# Revit family: HL_Dachablauf_HL64.1F-B-221103
name_source: partatom
category: Instalační zařizovací předměty
units: mm (PartAtom-declared; Revit-internal decimal feet)

## family parameters
Bod výpočtu místnosti = Ano
Kóta kulaté spojky = Použít průměr
Nadpis OmniClass = Deck Waste Water Drains
Ořezat dutým tvarem při načtení = Ne
Sdílené = Ne
Typ dílu = Normální
Vždy vertikální = Ano
Založené na pracovní rovině = Ne
Číslo OmniClass = 23.70.50.21.24.14

## types (2) — shared parameters
EINLAUFROST = Laubfangkorb d 145 mm
MATERIAL = PP
Popis = Dachabläufe
Přípoj CW = Ne
Přípoj HW = Ne
Přípoj odpadních dílů = Ano
Přípoj ventilace = Ne
URL = http://www.hutterer-lechner.com
Výrobce = HL Hutterer & Lechner GmbH
zero-valued in all types: Výchozí výška

## per-type parameters (varying)
| type | DIMENSION | DURCHMESSER | EAN | GEWICHT | Indexovaná poznámka | Komentáře k typům | LEISTUNG | Model |
| HL_Dachablauf_HL64.1F_1 | DN110 | 110 mm | 9003076031641 | 0,988 [kg] | HL64.1F_1 | HL64.1F/1 Dachablauf DN110 waagrecht mit PP_Kragen und Heizung (10_30W/230V), | 7,8l/s | HL64.1F_1 |
| HL_Dachablauf_HL64.1F_7 | DN75 | 75 mm | 9003076031665 | 0,877 [kg] | HL64.1F_7 | HL64.1F/7 Dachablauf DN75 waagrecht mit PP_Kragen und Heizung (10_30W/230V), | 6,9l/s | HL64.1F_7 |

## geometry (parser evidence)
native form markers: Sweep x15
no freeform markers — native parametric forms only
